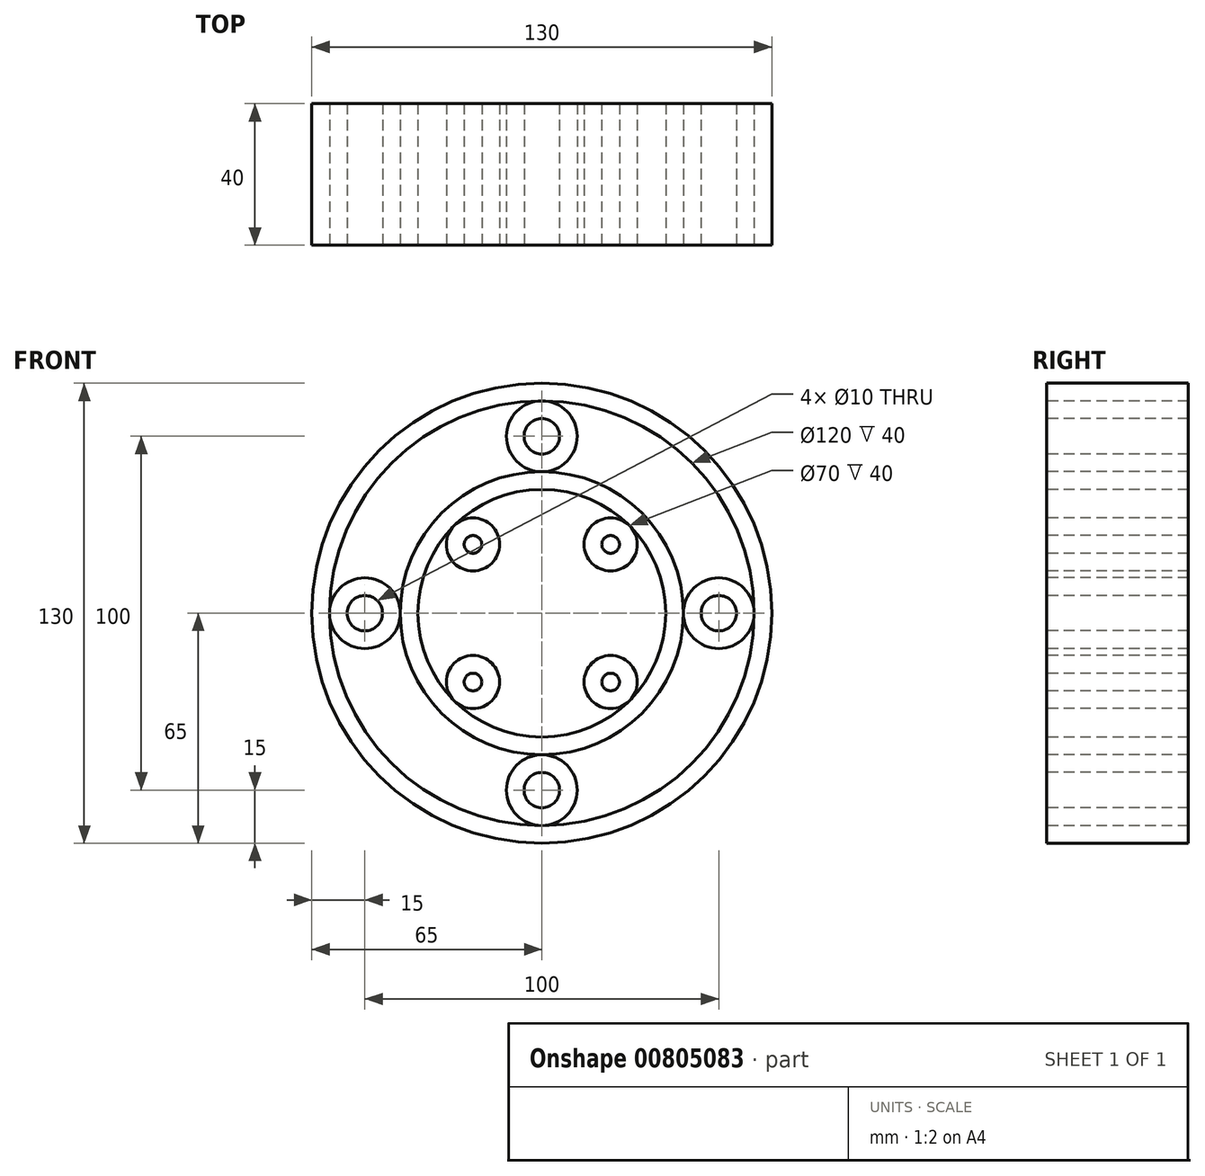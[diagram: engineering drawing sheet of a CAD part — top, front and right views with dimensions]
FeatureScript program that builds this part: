
annotation { "Feature Type Name" : "Feature", "Feature Type Description" : "" }
export const myFeature = defineFeature(function(context is Context, id is Id, definition is map)
    precondition{}
    {
        {
            var Q0;
            Q0=qCreatedBy(makeId("Front.planeOp"),FACE);
            var sketch = newSketch(context, id + "F0", { "sketchPlane" : qUnion([Q0])});
            skCircle(sketch, "E0", {"center": v(0, 0) * mm, "radius": 60 * mm});
            skCircle(sketch, "E1", {"center": v(0, 0) * mm, "radius": 40 * mm});
            skCircle(sketch, "E2", {"center": v(0, 0) * mm, "radius": 50 * mm, "construction": true});
            skCircle(sketch, "E3", {"center": v(0, 50) * mm, "radius": 10 * mm});
            skCircle(sketch, "E4", {"center": v(50, 0) * mm, "radius": 10 * mm});
            skCircle(sketch, "E5", {"center": v(0, -50) * mm, "radius": 10 * mm});
            skCircle(sketch, "E6", {"center": v(-50, 0) * mm, "radius": 10 * mm});
            skCircle(sketch, "E7", {"center": v(0, 0) * mm, "radius": 65 * mm});
            skCircle(sketch, "E8", {"center": v(0, 0) * mm, "radius": 35 * mm});
            skCircle(sketch, "E9", {"center": v(0, 50) * mm, "radius": 5 * mm});
            skCircle(sketch, "E10", {"center": v(50, 0) * mm, "radius": 5 * mm});
            skCircle(sketch, "E11", {"center": v(0, -50) * mm, "radius": 5 * mm});
            skCircle(sketch, "E12", {"center": v(-50, 0) * mm, "radius": 5 * mm});
            skCircle(sketch, "E13", {"center": v(0, 0) * mm, "radius": 20 * mm});
            skCircle(sketch, "E14", {"center": v(0, 0) * mm, "radius": 27.5 * mm, "construction": true});
            skLineSegment(sketch, "E15", {"start": v(19.45, 19.45) * mm, "end": v(0, 0) * mm, "construction": true});
            skLineSegment(sketch, "E16", {"start": v(0, 0) * mm, "end": v(-19.45, -19.45) * mm, "construction": true});
            skLineSegment(sketch, "E17", {"start": v(0, 0) * mm, "end": v(-19.45, 19.45) * mm, "construction": true});
            skLineSegment(sketch, "E18", {"start": v(0, 0) * mm, "end": v(19.45, -19.45) * mm, "construction": true});
            skCircle(sketch, "E19", {"center": v(-19.45, 19.45) * mm, "radius": 7.5 * mm});
            skCircle(sketch, "E20", {"center": v(19.45, 19.45) * mm, "radius": 7.5 * mm});
            skCircle(sketch, "E21", {"center": v(19.45, -19.45) * mm, "radius": 7.5 * mm});
            skCircle(sketch, "E22", {"center": v(-19.45, -19.45) * mm, "radius": 7.5 * mm});
            skCircle(sketch, "E23", {"center": v(19.45, 19.45) * mm, "radius": 2.5 * mm});
            skCircle(sketch, "E24", {"center": v(-19.45, 19.45) * mm, "radius": 2.5 * mm});
            skCircle(sketch, "E25", {"center": v(-19.45, -19.45) * mm, "radius": 2.5 * mm});
            skCircle(sketch, "E26", {"center": v(19.45, -19.45) * mm, "radius": 2.5 * mm});
            skSolve(sketch);
        }
        {
            var Q0;
            Q0=makeQuery(id+"F0.imprint","IMPRINT",FACE,{"disambiguationData":[TD([[makeQuery(id+"F0.imprint","IMPRINT",EDGE,{"derivedFrom":sQuery(id+"F0.wireOp",EDGE,"E9")}),-1.0]])]});
            var Q1;
            Q1=makeQuery(id+"F0.imprint","IMPRINT",FACE,{"disambiguationData":[TD([[makeQuery(id+"F0.imprint","IMPRINT",EDGE,{"derivedFrom":sQuery(id+"F0.wireOp",EDGE,"E7")}),1.0]])]});
            var Q2;
            Q2=makeQuery(id+"F0.imprint","IMPRINT",FACE,{"disambiguationData":[TD([[makeQuery(id+"F0.imprint","IMPRINT",EDGE,{"derivedFrom":sQuery(id+"F0.wireOp",EDGE,"E12")}),-1.0]])]});
            var Q3;
            Q3=makeQuery(id+"F0.imprint","IMPRINT",FACE,{"disambiguationData":[TD([[makeQuery(id+"F0.imprint","IMPRINT",EDGE,{"derivedFrom":sQuery(id+"F0.wireOp",EDGE,"E8")}),-1.0]])]});
            var Q4;
            Q4=makeQuery(id+"F0.imprint","IMPRINT",FACE,{"disambiguationData":[TD([[makeQuery(id+"F0.imprint","IMPRINT",EDGE,{"derivedFrom":sQuery(id+"F0.wireOp",EDGE,"E10")}),-1.0]])]});
            var Q5;
            Q5=makeQuery(id+"F0.imprint","IMPRINT",FACE,{"disambiguationData":[TD([[makeQuery(id+"F0.imprint","IMPRINT",EDGE,{"derivedFrom":sQuery(id+"F0.wireOp",EDGE,"E11")}),-1.0]])]});
            var Q6;
            Q6=makeQuery(id+"F0.imprint","IMPRINT",FACE,{"disambiguationData":[TD([[makeQuery(id+"F0.imprint","IMPRINT",EDGE,{"derivedFrom":sQuery(id+"F0.wireOp",EDGE,"E24")}),-1.0]])]});
            var Q7;
            Q7=makeQuery(id+"F0.imprint","IMPRINT",FACE,{"disambiguationData":[TD([[makeQuery(id+"F0.imprint","IMPRINT",EDGE,{"derivedFrom":sQuery(id+"F0.wireOp",EDGE,"E23")}),-1.0]])]});
            var Q8;
            Q8=makeQuery(id+"F0.imprint","IMPRINT",FACE,{"disambiguationData":[TD([[makeQuery(id+"F0.imprint","IMPRINT",EDGE,{"derivedFrom":sQuery(id+"F0.wireOp",EDGE,"E26")}),-1.0]])]});
            var Q9;
            Q9=makeQuery(id+"F0.imprint","IMPRINT",FACE,{"disambiguationData":[TD([[makeQuery(id+"F0.imprint","IMPRINT",EDGE,{"derivedFrom":sQuery(id+"F0.wireOp",EDGE,"E25")}),-1.0]])]});
            var Q10;
            {var subQ0=sQuery(id+"F0.wireOp",EDGE,"E13");var subQ4=makeQuery(id+"F0.imprint","IMPRINT",VERTEX,{"derivedFrom":subQ0});Q10=makeQuery(id+"F0.imprint","IMPRINT",FACE,{"disambiguationData":[TD([[makeQuery(id+"F0.imprint","IMPRINT",EDGE,{"disambiguationData":[TD([[subQ4,1.0]])],"derivedFrom":subQ0}),1.0]])]});}
            extrude(context, id + "F1", {"entities" : qUnion([Q0, Q1, Q2, Q3, Q4, Q5, Q6, Q7, Q8, Q9, Q10]), "endBound" : BoundingType.SYMMETRIC, "oppositeDirection" : true, "depth" : 40 * mm, "offsetDistance" : 25 * mm});
        }
    });
